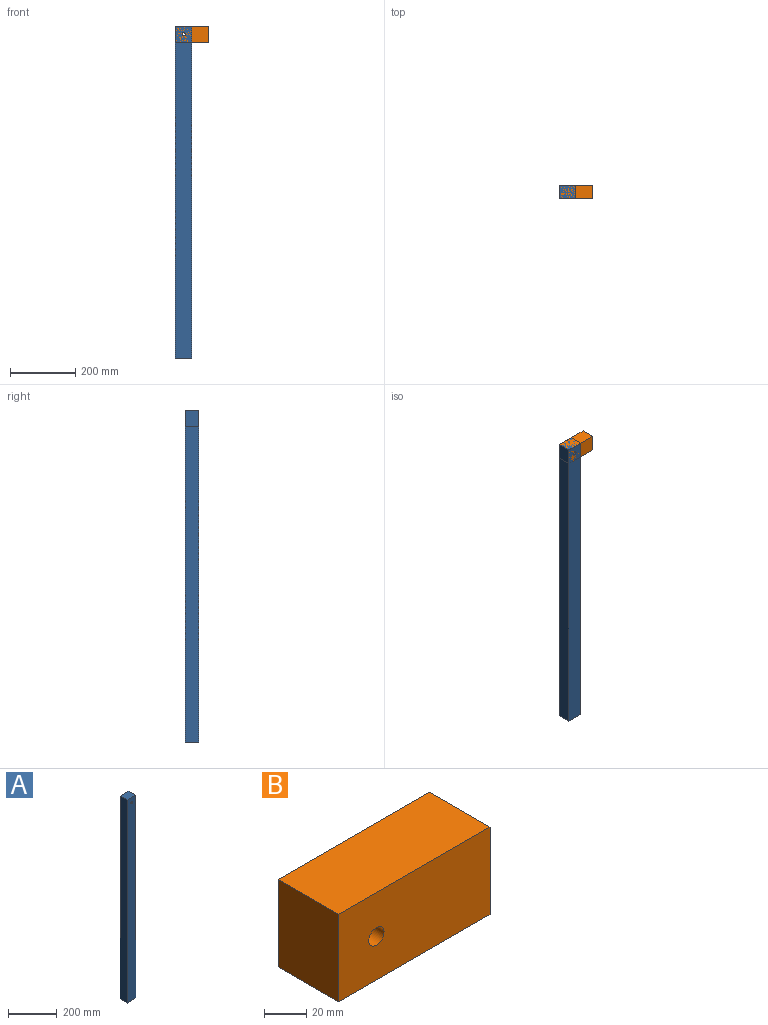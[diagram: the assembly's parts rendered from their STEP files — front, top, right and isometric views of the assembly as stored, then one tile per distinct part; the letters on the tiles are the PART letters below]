
ASSEMBLY  parts=2 mates=1
PART A: 7 faces, bbox 50.8x40.6x1016 mm
  f0: plane 50.8x40.64mm, normal (0,0,-1), area 2064.5mm2, adj f1,f4,f5,f6
  f1: plane 1016x40.64mm, normal (1,0,0), area 41290.2mm2, adj f0,f2,f5,f6
  f2: plane 50.8x40.64mm, normal (0,0,1), area 2064.5mm2, adj f1,f4,f5,f6
  f3: cylinder r=5.08mm len=40.64mm, axis (0,-1,0), area 1297.2mm2, adj f5,f6
  f4: plane 1016x40.64mm, normal (-1,0,0), area 41290.2mm2, adj f0,f2,f5,f6
  f5: plane 1016x50.8mm, normal (0,1,0), area 51531.7mm2, adj f0,f1,f2,f3,f4
  f6: plane 1016x50.8mm, normal (0,-1,0), area 51531.7mm2, adj f0,f1,f2,f3,f4
PART B: 7 faces, bbox 101.6x40.6x50.8 mm
  f0: plane 50.8x40.64mm, normal (-1,0,0), area 2064.5mm2, adj f1,f4,f5,f6
  f1: plane 101.6x40.64mm, normal (0,0,-1), area 4129mm2, adj f0,f2,f5,f6
  f2: plane 50.8x40.64mm, normal (1,0,0), area 2064.5mm2, adj f1,f4,f5,f6
  f3: cylinder r=5.08mm len=40.64mm, axis (0,-1,0), area 1297.2mm2, adj f5,f6
  f4: plane 101.6x40.64mm, normal (0,0,1), area 4129mm2, adj f0,f2,f5,f6
  f5: plane 101.6x50.8mm, normal (0,1,0), area 5080.2mm2, adj f0,f1,f2,f3,f4
  f6: plane 101.6x50.8mm, normal (0,-1,0), area 5080.2mm2, adj f0,f1,f2,f3,f4
PLACE A t=(-1200.15,-560.23,-390.33)mm
PLACE B t=(-1289.21,-560.23,-390.33)mm
MATE revolute B.f3 <-> A.f3  axis (0,-1,0) through (-1200.15,-585.63,92.27)mm
